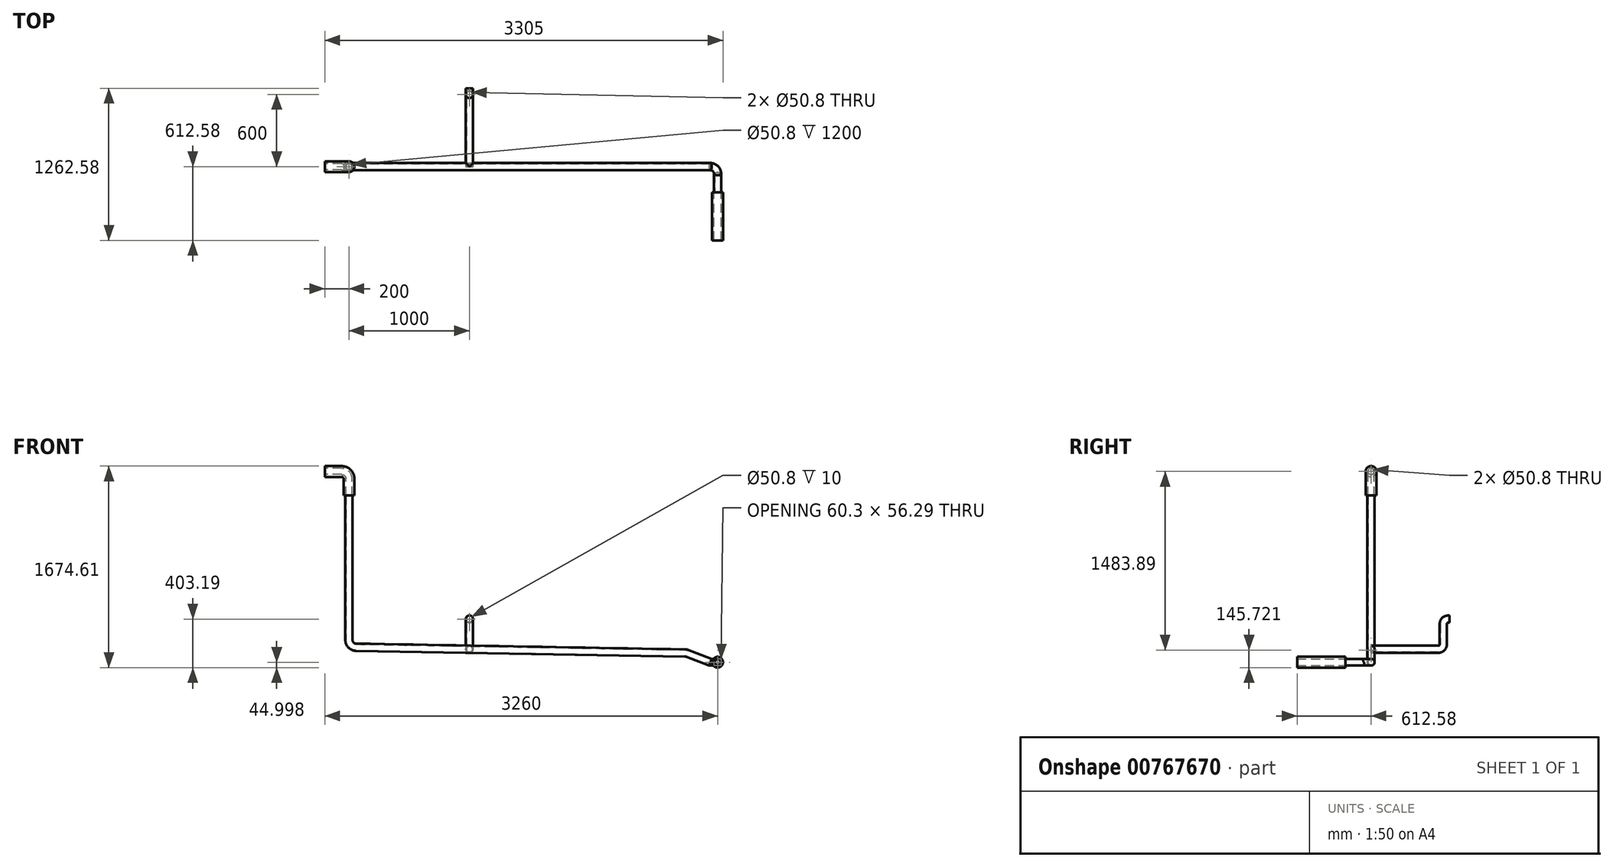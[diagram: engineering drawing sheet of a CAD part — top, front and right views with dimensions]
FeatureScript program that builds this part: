
annotation { "Feature Type Name" : "Feature", "Feature Type Description" : "" }
export const myFeature = defineFeature(function(context is Context, id is Id, definition is map)
    precondition{}
    {
        {
            var Q0;
            Q0=qCreatedBy(makeId("Right.planeOp"),FACE);
            var sketch = newSketch(context, id + "F0", { "sketchPlane" : qUnion([Q0])});
            skLineSegment(sketch, "E0", {"start": v(0, 0) * mm, "end": v(-10, 0) * mm});
            skLineSegment(sketch, "E1", {"start": v(-50, -40) * mm, "end": v(-50, -210) * mm});
            skPoint(sketch, "E2.visualSharp", {"position": v(-50, 0) * mm});
            skArc(sketch, "E2.filletArc", {"start": v(-10, 0) * mm, "mid": v(-38.28, -11.72) * mm, "end": v(-50, -40) * mm});
            skLineSegment(sketch, "E3", {"start": v(-90, -250) * mm, "end": v(-650, -250) * mm});
            skPoint(sketch, "E4.visualSharp", {"position": v(-50, -250) * mm});
            skArc(sketch, "E4.filletArc", {"start": v(-90, -250) * mm, "mid": v(-61.72, -238.28) * mm, "end": v(-50, -210) * mm});
            skSolve(sketch);
        }
        {
            var Q0;
            Q0=qCreatedBy(makeId("Front.planeOp"),FACE);
            var sketch = newSketch(context, id + "F1", { "sketchPlane" : qUnion([Q0])});
            skCircle(sketch, "E5", {"center": v(0, 0) * mm, "radius": 25.4 * mm});
            skCircle(sketch, "E6", {"center": v(0, 0) * mm, "radius": 30 * mm});
            skSolve(sketch);
        }
        {
            var Q0;
            Q0=makeQuery(id+"F1.imprint","IMPRINT",FACE,{"disambiguationData":[TD([[makeQuery(id+"F1.imprint","IMPRINT",EDGE,{"derivedFrom":sQuery(id+"F1.wireOp",EDGE,"E5")}),-1.0]])]});
            var Q1;
            Q1=sQuery(id+"F0.wireOp",EDGE,"E0");
            var Q2;
            Q2=sQuery(id+"F0.wireOp",EDGE,"E2.filletArc");
            var Q3;
            Q3=sQuery(id+"F0.wireOp",EDGE,"E1");
            var Q4;
            Q4=sQuery(id+"F0.wireOp",EDGE,"E4.filletArc");
            var Q5;
            Q5=sQuery(id+"F0.wireOp",EDGE,"E3");
            sweep(context, id + "F2", {"profiles" : qUnion([Q0]), "path" : qUnion([Q1, Q2, Q3, Q4, Q5])});
        }
        {
            var Q0;
            Q0=makeQuery(id+"F2.opSweep","CAP_FACE",FACE,{"disambiguationData":[OSD([sQuery(id+"F0.wireOp",VERTEX,"E3.end"),sQuery(id+"F1.wireOp",EDGE,"E5"),sQuery(id+"F1.wireOp",EDGE,"E6")])],"isStart":false});
            var sketch = newSketch(context, id + "F3", { "sketchPlane" : qUnion([Q0])});
            skCircle(sketch, "E7.0", {"center": v(0, -250) * mm, "radius": 25.4 * mm});
            skLineSegment(sketch, "E8", {"start": v(-30, -210) * mm, "end": v(-30, -40) * mm});
            skLineSegment(sketch, "E9", {"start": v(30, -40) * mm, "end": v(30, -210) * mm});
            skLineSegment(sketch, "E10", {"start": v(-941.05, -233.57) * mm, "end": v(1789.42, -281.23) * mm});
            skLineSegment(sketch, "E11", {"start": v(-1000, -173.58) * mm, "end": v(-1000, 1026.42) * mm});
            skLineSegment(sketch, "E12", {"start": v(1809.88, -285.21) * mm, "end": v(2000, -358.2) * mm});
            skPoint(sketch, "E13.visualSharp", {"position": v(-1000, -232.54) * mm});
            skArc(sketch, "E13.filletArc", {"start": v(-1000, -173.58) * mm, "mid": v(-982.8, -215.64) * mm, "end": v(-941.05, -233.57) * mm});
            skPoint(sketch, "E14.visualSharp", {"position": v(1800, -281.42) * mm});
            skArc(sketch, "E14.filletArc", {"start": v(1809.88, -285.21) * mm, "mid": v(1799.82, -282.33) * mm, "end": v(1789.42, -281.23) * mm});
            skSolve(sketch);
        }
        {
            var Q0;
            Q0=qCreatedBy(makeId("Top.planeOp"),FACE);
            var Q1;
            Q1=sQuery(id+"F3.wireOp",VERTEX,"E11.end");
            cPlane(context, id + "F4", {"entities" : qUnion([Q0, Q1]), "cplaneType" : CPlaneType.PLANE_POINT, "offset" : 25 * mm, "width" : 150 * mm, "height" : 150 * mm});
        }
        {
            var Q0;
            Q0=qCreatedBy(id+"F4.planeOp",FACE);
            var sketch = newSketch(context, id + "F5", { "sketchPlane" : qUnion([Q0])});
            skPoint(sketch, "E15.0", {"position": v(-1000, -650) * mm});
            skCircle(sketch, "E16", {"center": v(-1000, -650) * mm, "radius": 25.4 * mm});
            skCircle(sketch, "E17", {"center": v(-1000, -650) * mm, "radius": 30.15 * mm});
            skSolve(sketch);
        }
        {
            var Q0;
            Q0=makeQuery(id+"F5.imprint","IMPRINT",FACE,{"disambiguationData":[TD([[makeQuery(id+"F5.imprint","IMPRINT",EDGE,{"derivedFrom":sQuery(id+"F5.wireOp",EDGE,"E16")}),-1.0]])]});
            var Q1;
            Q1=sQuery(id+"F3.wireOp",EDGE,"E11");
            var Q2;
            Q2=sQuery(id+"F3.wireOp",EDGE,"E13.filletArc");
            var Q3;
            Q3=sQuery(id+"F3.wireOp",EDGE,"E10");
            var Q4;
            Q4=sQuery(id+"F3.wireOp",EDGE,"E12");
            var Q5;
            Q5=sQuery(id+"F3.wireOp",EDGE,"E14.filletArc");
            sweep(context, id + "F6", {"operationType" : NewBodyOperationType.ADD, "profiles" : qUnion([Q0]), "path" : qUnion([Q1, Q2, Q3, Q4, Q5])});
        }
        {
            var Q0;
            Q0=makeQuery(id+"F6.opSweep","CAP_FACE",FACE,{"disambiguationData":[OSD([sQuery(id+"F3.wireOp",VERTEX,"E12.end"),sQuery(id+"F5.wireOp",EDGE,"E16"),sQuery(id+"F5.wireOp",EDGE,"E17")])],"isStart":false});
            var sketch = newSketch(context, id + "F7", { "sketchPlane" : qUnion([Q0])});
            skPoint(sketch, "E18", {"position": v(-650, 382.33) * mm});
            skSolve(sketch);
        }
        {
            var Q0;
            Q0=qCreatedBy(makeId("Top.planeOp"),FACE);
            var Q1;
            Q1=sQuery(id+"F7.wireOp",VERTEX,"E18");
            cPlane(context, id + "F8", {"entities" : qUnion([Q0, Q1]), "cplaneType" : CPlaneType.PLANE_POINT, "offset" : 25 * mm, "width" : 150 * mm, "height" : 150 * mm});
        }
        {
            var Q0;
            Q0=qCreatedBy(id+"F8.planeOp",FACE);
            var sketch = newSketch(context, id + "F9", { "sketchPlane" : qUnion([Q0])});
            skPoint(sketch, "E19.0", {"position": v(2000, -650) * mm});
            skLineSegment(sketch, "E20", {"start": v(2000, -650) * mm, "end": v(2000, -650) * mm});
            skLineSegment(sketch, "E21", {"start": v(2060, -710) * mm, "end": v(2060, -900) * mm});
            skPoint(sketch, "E22.visualSharp", {"position": v(2060, -650) * mm});
            skArc(sketch, "E22.filletArc", {"start": v(2060, -710) * mm, "mid": v(2042.43, -667.57) * mm, "end": v(2000, -650) * mm});
            skSolve(sketch);
        }
        {
            var Q0;
            {var subQ0=sQuery(id+"F3.wireOp",VERTEX,"E12.end");Q0=makeQuery(id+"F7.imprint","IMPRINT",FACE,{"disambiguationData":[TD([[makeQuery(id+"F7.imprint","IMPRINT",EDGE,{"derivedFrom":makeQuery(id+"F6.opSweep","CAP_EDGE",EDGE,{"disambiguationData":[OSD([subQ0,sQuery(id+"F5.wireOp",EDGE,"E16")])],"isStart":false})}),1.0]])]});}
            var Q1;
            Q1=sQuery(id+"F9.wireOp",EDGE,"E22.filletArc");
            var Q2;
            Q2=sQuery(id+"F9.wireOp",EDGE,"E21");
            sweep(context, id + "F10", {"operationType" : NewBodyOperationType.ADD, "profiles" : qUnion([Q0]), "path" : qUnion([Q1, Q2])});
        }
        {
            var Q0;
            Q0=makeQuery(id+"F10.opSweep","CAP_FACE",FACE,{"disambiguationData":[OSD([sQuery(id+"F3.wireOp",VERTEX,"E12.end"),sQuery(id+"F5.wireOp",EDGE,"E16"),sQuery(id+"F5.wireOp",EDGE,"E17"),sQuery(id+"F9.wireOp",VERTEX,"E21.end")])],"isStart":false});
            var sketch = newSketch(context, id + "F11", { "sketchPlane" : qUnion([Q0])});
            skPoint(sketch, "E23", {"position": v(2060, -11.87) * mm});
            skSolve(sketch);
        }
        {
            var Q0;
            Q0=qCreatedBy(makeId("Right.planeOp"),FACE);
            var Q1;
            Q1=sQuery(id+"F11.wireOp",VERTEX,"E23");
            cPlane(context, id + "F12", {"entities" : qUnion([Q0, Q1]), "cplaneType" : CPlaneType.PLANE_POINT, "offset" : 25 * mm, "width" : 150 * mm, "height" : 150 * mm});
        }
        {
            var Q0;
            Q0=qCreatedBy(id+"F12.planeOp",FACE);
            var sketch = newSketch(context, id + "F13", { "sketchPlane" : qUnion([Q0])});
            skLineSegment(sketch, "E24.bottom", {"start": v(-1097.02, -256.22) * mm, "end": v(-862.58, -256.22) * mm});
            skLineSegment(sketch, "E24.top", {"start": v(-1097.02, -504.94) * mm, "end": v(-862.58, -504.94) * mm});
            skLineSegment(sketch, "E24.left", {"start": v(-1097.02, -256.22) * mm, "end": v(-1097.02, -504.94) * mm});
            skLineSegment(sketch, "E24.right", {"start": v(-862.58, -256.22) * mm, "end": v(-862.58, -504.94) * mm});
            skSolve(sketch);
        }
        {
            var Q0;
            Q0=makeQuery(id+"F13.imprint","IMPRINT",FACE,{"disambiguationData":[TD([[makeQuery(id+"F13.imprint","IMPRINT",EDGE,{"derivedFrom":sQuery(id+"F13.wireOp",EDGE,"E24.bottom")}),-1.0]])]});
            extrude(context, id + "F14", {"entities" : qUnion([Q0]), "operationType" : NewBodyOperationType.REMOVE, "endBound" : BoundingType.THROUGH_ALL, "oppositeDirection" : true, "depth" : 25 * mm, "offsetDistance" : 25 * mm, "hasSecondDirection" : true, "secondDirectionBound" : SecondDirectionBoundingType.THROUGH_ALL, "secondDirectionOppositeDirection" : false, "secondDirectionDepth" : 25 * mm});
        }
        {
            var Q0;
            Q0=qCreatedBy(id+"F4.planeOp",FACE);
            var sketch = newSketch(context, id + "F15", { "sketchPlane" : qUnion([Q0])});
            skCircle(sketch, "E25.0", {"center": v(-1000, -650) * mm, "radius": 25.4 * mm});
            skCircle(sketch, "E26", {"center": v(-1000, -650) * mm, "radius": 45 * mm});
            skSolve(sketch);
        }
        {
            var Q0;
            Q0=qCreatedBy(makeId("Front.planeOp"),FACE);
            var Q1;
            Q1=sQuery(id+"F15.wireOp",VERTEX,"E25.0.center");
            cPlane(context, id + "F16", {"entities" : qUnion([Q0, Q1]), "cplaneType" : CPlaneType.PLANE_POINT, "offset" : 25 * mm, "width" : 150 * mm, "height" : 150 * mm});
        }
        {
            var Q0;
            Q0=qCreatedBy(id+"F16.planeOp",FACE);
            var sketch = newSketch(context, id + "F17", { "sketchPlane" : qUnion([Q0])});
            skPoint(sketch, "E27.0", {"position": v(-1000, 1026.42) * mm});
            skLineSegment(sketch, "E28", {"start": v(-1000, 1026.42) * mm, "end": v(-1000, 1166.42) * mm});
            skLineSegment(sketch, "E29", {"start": v(-1060, 1226.42) * mm, "end": v(-1200, 1226.42) * mm});
            skPoint(sketch, "E30.visualSharp", {"position": v(-1000, 1226.42) * mm});
            skArc(sketch, "E30.filletArc", {"start": v(-1000, 1166.42) * mm, "mid": v(-1017.57, 1208.84) * mm, "end": v(-1060, 1226.42) * mm});
            skSolve(sketch);
        }
        {
            var Q0;
            Q0=makeQuery(id+"F15.imprint","IMPRINT",FACE,{"disambiguationData":[TD([[makeQuery(id+"F15.imprint","IMPRINT",EDGE,{"derivedFrom":sQuery(id+"F15.wireOp",EDGE,"E25.0")}),-1.0]])]});
            var Q1;
            Q1=sQuery(id+"F17.wireOp",EDGE,"E28");
            var Q2;
            Q2=sQuery(id+"F17.wireOp",EDGE,"E30.filletArc");
            var Q3;
            Q3=sQuery(id+"F17.wireOp",EDGE,"E29");
            sweep(context, id + "F18", {"profiles" : qUnion([Q0]), "path" : qUnion([Q1, Q2, Q3])});
        }
        {
            var Q0;
            Q0=makeQuery(id+"F14.boolean.opBoolean","COPY",FACE,{"derivedFrom":makeQuery(id+"F14.opExtrude","SWEPT_FACE",FACE,{"disambiguationData":[OSD([sQuery(id+"F13.wireOp",EDGE,"E24.right")])]})});
            var sketch = newSketch(context, id + "F19", { "sketchPlane" : qUnion([Q0])});
            skFitSpline(sketch, "E31.0", {"points": [v(2061.22, -334.5) * mm, v(2059.6, -334.46) * mm, v(2057.98, -334.53) * mm, v(2056.37, -334.71) * mm, v(2054.77, -334.97) * mm, v(2052.81, -335.41) * mm, v(2050.53, -336.15) * mm, v(2048.7, -336.94) * mm, v(2047.25, -337.67) * mm, v(2045.85, -338.48) * mm, v(2044.18, -339.59) * mm, v(2042.33, -341.1) * mm, v(2040.9, -342.52) * mm, v(2039.85, -343.74) * mm, v(2038.85, -345.01) * mm, v(2037.75, -346.68) * mm, v(2036.82, -348.45) * mm, v(2036.18, -349.92) * mm, v(2035.76, -351.07) * mm, v(2035.4, -352.22) * mm, v(2035.02, -353.78) * mm, v(2034.76, -355.36) * mm, v(2034.62, -356.96) * mm, v(2034.59, -358.17) * mm, v(2034.62, -359.39) * mm, v(2034.75, -360.99) * mm, v(2035.08, -362.96) * mm, v(2035.61, -364.9) * mm, v(2036.17, -366.43) * mm, v(2036.8, -367.9) * mm, v(2037.73, -369.68) * mm, v(2038.84, -371.35) * mm, v(2039.84, -372.63) * mm, v(2040.9, -373.85) * mm, v(2042.32, -375.27) * mm, v(2043.87, -376.54) * mm, v(2045.2, -377.47) * mm, v(2046.56, -378.34) * mm, v(2048.32, -379.3) * mm, v(2050.17, -380.08) * mm, v(2051.68, -380.6) * mm, v(2052.85, -380.95) * mm, v(2054.02, -381.25) * mm, v(2055.6, -381.57) * mm, v(2057.58, -381.83) * mm, v(2059.58, -381.92) * mm, v(2061.2, -381.89) * mm, v(2062.82, -381.78) * mm, v(2064.8, -381.51) * mm, v(2067.14, -380.99) * mm, v(2069.43, -380.25) * mm, v(2071.67, -379.3) * mm, v(2073.79, -378.15) * mm, v(2075.78, -376.82) * mm, v(2077.33, -375.56) * mm, v(2078.52, -374.44) * mm, v(2079.63, -373.28) * mm, v(2080.9, -371.73) * mm, v(2082.01, -370.07) * mm, v(2082.8, -368.67) * mm, v(2083.34, -367.58) * mm, v(2083.82, -366.47) * mm, v(2084.37, -364.96) * mm, v(2084.8, -363.42) * mm, v(2085.1, -361.85) * mm, v(2085.27, -360.65) * mm, v(2085.38, -359.43) * mm, v(2085.42, -357.82) * mm, v(2085.32, -355.82) * mm, v(2085, -353.84) * mm, v(2084.6, -352.27) * mm, v(2084.13, -350.72) * mm, v(2083.4, -348.86) * mm, v(2082.47, -347.08) * mm, v(2081.6, -345.7) * mm, v(2080.68, -344.38) * mm, v(2079.4, -342.83) * mm, v(2077.98, -341.41) * mm, v(2076.76, -340.36) * mm, v(2075.48, -339.36) * mm, v(2073.8, -338.25) * mm, v(2072.05, -337.3) * mm, v(2070.58, -336.63) * mm, v(2069.46, -336.17) * mm, v(2068.3, -335.77) * mm, v(2066.77, -335.32) * mm, v(2064.82, -334.87) * mm, v(2062.83, -334.6) * mm, v(2061.22, -334.5) * mm, v(2059.6, -334.46) * mm, v(2057.98, -334.53) * mm, v(2061.22, -334.5) * mm]});
            skFitSpline(sketch, "E32.0", {"points": [v(2058.56, -330.07) * mm, v(2060.48, -330.02) * mm, v(2062.4, -330.1) * mm, v(2064.3, -330.32) * mm, v(2066.2, -330.62) * mm, v(2068.53, -331.15) * mm, v(2071.24, -332.03) * mm, v(2073.42, -332.96) * mm, v(2075.13, -333.83) * mm, v(2076.8, -334.79) * mm, v(2078.77, -336.11) * mm, v(2080.97, -337.91) * mm, v(2082.66, -339.59) * mm, v(2083.92, -341.04) * mm, v(2084.8, -342.17) * mm, v(2085.63, -343.34) * mm, v(2086.38, -344.54) * mm, v(2087.08, -345.79) * mm, v(2087.7, -347.06) * mm, v(2088.27, -348.38) * mm, v(2088.77, -349.74) * mm, v(2089.2, -351.1) * mm, v(2089.65, -352.96) * mm, v(2089.96, -354.83) * mm, v(2090.12, -356.73) * mm, v(2090.16, -358.16) * mm, v(2090.12, -359.6) * mm, v(2089.97, -361.51) * mm, v(2089.59, -363.86) * mm, v(2088.95, -366.15) * mm, v(2088.29, -367.97) * mm, v(2087.54, -369.72) * mm, v(2086.43, -371.83) * mm, v(2085.11, -373.82) * mm, v(2083.93, -375.34) * mm, v(2082.67, -376.78) * mm, v(2080.99, -378.46) * mm, v(2079.15, -379.97) * mm, v(2077.58, -381.07) * mm, v(2075.95, -382.1) * mm, v(2073.86, -383.24) * mm, v(2071.67, -384.17) * mm, v(2069.87, -384.8) * mm, v(2068.5, -385.21) * mm, v(2067.1, -385.56) * mm, v(2065.22, -385.94) * mm, v(2062.87, -386.25) * mm, v(2060.5, -386.36) * mm, v(2058.58, -386.32) * mm, v(2056.66, -386.2) * mm, v(2054.3, -385.87) * mm, v(2051.52, -385.25) * mm, v(2048.8, -384.37) * mm, v(2046.14, -383.24) * mm, v(2043.64, -381.88) * mm, v(2041.27, -380.3) * mm, v(2039.42, -378.8) * mm, v(2038.02, -377.48) * mm, v(2037.03, -376.44) * mm, v(2036.1, -375.37) * mm, v(2035.22, -374.25) * mm, v(2034.4, -373.08) * mm, v(2033.64, -371.88) * mm, v(2032.94, -370.63) * mm, v(2032.3, -369.33) * mm, v(2031.73, -368.01) * mm, v(2031.07, -366.23) * mm, v(2030.56, -364.4) * mm, v(2030.2, -362.53) * mm, v(2030, -361.1) * mm, v(2029.88, -359.66) * mm, v(2029.82, -357.76) * mm, v(2029.95, -355.38) * mm, v(2030.33, -353.03) * mm, v(2030.8, -351.16) * mm, v(2031.35, -349.33) * mm, v(2032.23, -347.11) * mm, v(2033.33, -345) * mm, v(2034.35, -343.37) * mm, v(2035.46, -341.8) * mm, v(2036.97, -339.96) * mm, v(2038.65, -338.28) * mm, v(2040.1, -337.02) * mm, v(2041.63, -335.84) * mm, v(2043.6, -334.52) * mm, v(2045.7, -333.38) * mm, v(2047.44, -332.6) * mm, v(2048.78, -332.06) * mm, v(2050.14, -331.58) * mm, v(2051.96, -331.04) * mm, v(2054.28, -330.51) * mm, v(2056.64, -330.2) * mm, v(2058.56, -330.07) * mm, v(2060.48, -330.02) * mm, v(2062.4, -330.1) * mm, v(2058.56, -330.07) * mm]});
            skCircle(sketch, "E33", {"center": v(2060, -358.2) * mm, "radius": 45 * mm});
            skSolve(sketch);
        }
        {
            var Q0;
            Q0=qCreatedBy(id+"F12.planeOp",FACE);
            var sketch = newSketch(context, id + "F20", { "sketchPlane" : qUnion([Q0])});
            skPoint(sketch, "E34.0", {"position": v(-862.58, -358.2) * mm});
            skLineSegment(sketch, "E35", {"start": v(-862.58, -358.2) * mm, "end": v(-1262.58, -358.2) * mm});
            skSolve(sketch);
        }
        {
            var Q0;
            Q0=makeQuery(id+"F19.imprint","IMPRINT",FACE,{"disambiguationData":[TD([[makeQuery(id+"F19.imprint","IMPRINT",EDGE,{"derivedFrom":sQuery(id+"F19.wireOp",EDGE,"E33")}),1.0]])]});
            var Q1;
            Q1=sQuery(id+"F20.wireOp",EDGE,"E35");
            sweep(context, id + "F21", {"profiles" : qUnion([Q0]), "path" : qUnion([Q1])});
        }
    });
